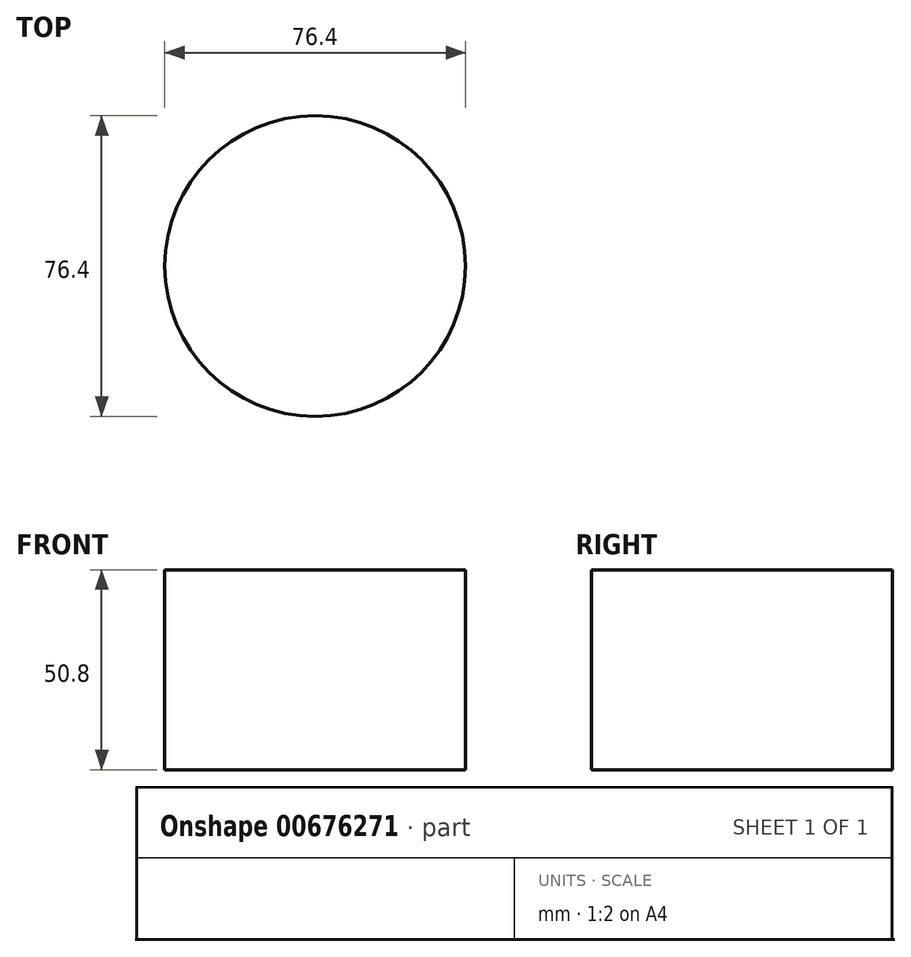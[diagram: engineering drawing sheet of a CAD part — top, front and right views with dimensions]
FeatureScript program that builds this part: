
annotation { "Feature Type Name" : "Feature", "Feature Type Description" : "" }
export const myFeature = defineFeature(function(context is Context, id is Id, definition is map)
    precondition{}
    {
        {
            var Q0;
            Q0=qCreatedBy(makeId("Top.planeOp"),FACE);
            var sketch = newSketch(context, id + "F0", { "sketchPlane" : qUnion([Q0])});
            skCircle(sketch, "E0", {"center": v(0, 0) * mm, "radius": 38.2 * mm});
            skSolve(sketch);
        }
        {
            var Q0;
            Q0=makeQuery(id+"F0.imprint","IMPRINT",FACE,{"disambiguationData":[TD([[makeQuery(id+"F0.imprint","IMPRINT",EDGE,{"derivedFrom":sQuery(id+"F0.wireOp",EDGE,"E0")}),1.0]])]});
            extrude(context, id + "F1", {"entities" : qUnion([Q0]), "depth" : 50.8 * mm, "offsetDistance" : 25.4 * mm});
        }
    });
